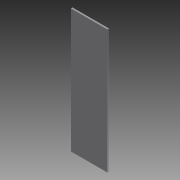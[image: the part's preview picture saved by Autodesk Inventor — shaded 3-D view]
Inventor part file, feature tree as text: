
AUTODESK INVENTOR PART (.ipt)
format: ipt  version: 2011 (Build 150239000, 239)  size: 64,000 bytes
history: native  units: in
note: dims shown in document units (in); Inventor stores cm internally (conversion verified against a paired STEP export)
features: extrude x1, sketch x1
ambient origin geometry x8: Origin, YZ Plane, XZ Plane, XY Plane, X Axis, Y Axis, Z Axis, Center Point
bodies: Solid1 (feature_tree)
feature tree (2):
  extrude  "Extrusion1"  Depth=19.5in
  sketch  "Sketch1"  dims[d0=5.75in d1=19.5in d2=0.25in d3=0.0in]
